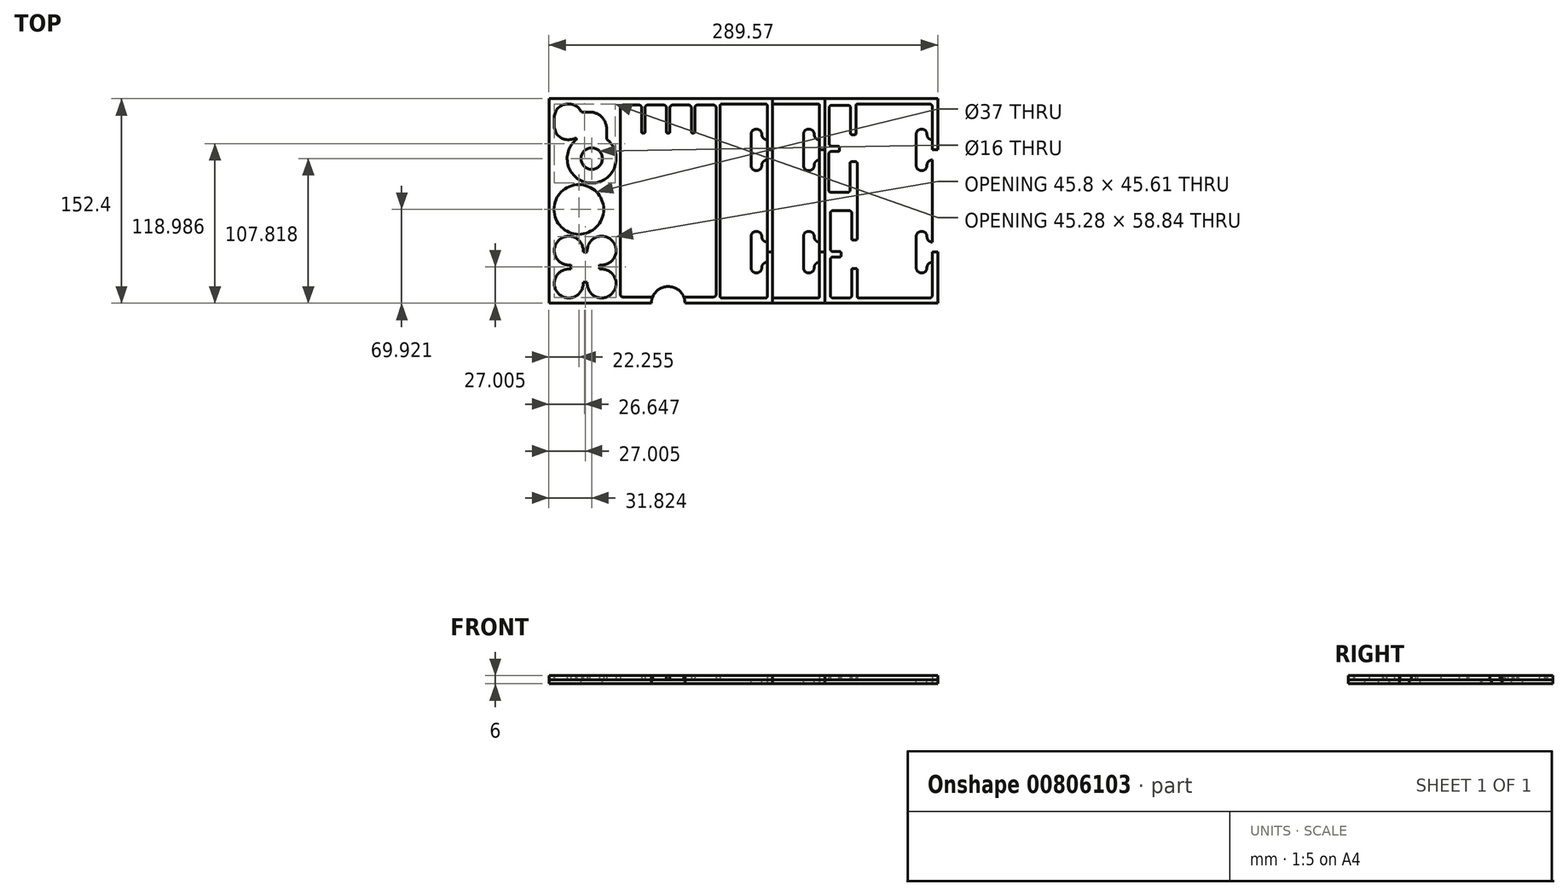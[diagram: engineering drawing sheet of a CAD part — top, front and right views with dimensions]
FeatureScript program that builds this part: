
annotation { "Feature Type Name" : "Feature", "Feature Type Description" : "" }
export const myFeature = defineFeature(function(context is Context, id is Id, definition is map)
    precondition{}
    {
        {
            var Q0;
            Q0=qCreatedBy(makeId("Top.planeOp"),FACE);
            var sketch = newSketch(context, id + "F0", { "sketchPlane" : qUnion([Q0])});
            skLineSegment(sketch, "E0.bottom", {"start": v(-142.07, 76.21) * mm, "end": v(147.5, 76.21) * mm});
            skLineSegment(sketch, "E0.top", {"start": v(-142.07, -76.19) * mm, "end": v(147.5, -76.19) * mm});
            skCircle(sketch, "E1", {"center": v(-127.32, -61.44) * mm, "radius": 10.75 * mm});
            skCircle(sketch, "E2", {"center": v(-102.82, -61.44) * mm, "radius": 10.75 * mm});
            skCircle(sketch, "E3", {"center": v(-127.32, -36.94) * mm, "radius": 10.75 * mm});
            skCircle(sketch, "E4", {"center": v(-102.82, -36.94) * mm, "radius": 10.75 * mm});
            skCircle(sketch, "E5", {"center": v(-119.82, -6.27) * mm, "radius": 18.5 * mm});
            skCircle(sketch, "E6", {"center": v(-115.07, -49.79) * mm, "radius": 10.75 * mm});
            skLineSegment(sketch, "E7", {"start": v(-138.07, 62.21) * mm, "end": v(-138.07, 55.71) * mm});
            skLineSegment(sketch, "E8", {"start": v(-117.07, 62.21) * mm, "end": v(-117.07, 55.71) * mm});
            skLineSegment(sketch, "E9", {"start": v(-128.07, 72.21) * mm, "end": v(-127.07, 72.21) * mm});
            skLineSegment(sketch, "E10", {"start": v(-128.07, 45.71) * mm, "end": v(-127.07, 45.71) * mm});
            skArc(sketch, "E11.filletArc", {"start": v(-128.07, 72.21) * mm, "mid": v(-135.14, 69.28) * mm, "end": v(-138.07, 62.21) * mm});
            skArc(sketch, "E12.filletArc", {"start": v(-117.07, 62.21) * mm, "mid": v(-120, 69.28) * mm, "end": v(-127.07, 72.21) * mm});
            skArc(sketch, "E13.filletArc", {"start": v(-127.07, 45.71) * mm, "mid": v(-120, 48.64) * mm, "end": v(-117.07, 55.71) * mm});
            skArc(sketch, "E14.filletArc", {"start": v(-138.07, 55.71) * mm, "mid": v(-135.14, 48.64) * mm, "end": v(-128.07, 45.71) * mm});
            skCircle(sketch, "E15", {"center": v(-110.25, 31.63) * mm, "radius": 18.25 * mm});
            skCircle(sketch, "E16", {"center": v(-110.25, 31.63) * mm, "radius": 8 * mm});
            skCircle(sketch, "E17", {"center": v(-111.62, 53.78) * mm, "radius": 12.5 * mm});
            skLineSegment(sketch, "E18", {"start": v(-111.83, 66.28) * mm, "end": v(-117.93, 66.28) * mm});
            skLineSegment(sketch, "E19", {"start": v(-99.12, 53.73) * mm, "end": v(-99.12, 46.1) * mm});
            skLineSegment(sketch, "E20", {"start": v(-89, 50.51) * mm, "end": v(-17.5, 50.51) * mm});
            skLineSegment(sketch, "E21", {"start": v(-73, 69.51) * mm, "end": v(-73, 51.51) * mm});
            skLineSegment(sketch, "E22", {"start": v(-70.5, 69.51) * mm, "end": v(-70.5, 51.51) * mm});
            skLineSegment(sketch, "E23", {"start": v(-54.5, 69.51) * mm, "end": v(-54.5, 51.51) * mm});
            skLineSegment(sketch, "E24", {"start": v(-52, 69.51) * mm, "end": v(-52, 51.51) * mm});
            skLineSegment(sketch, "E25", {"start": v(-36, 69.51) * mm, "end": v(-36, 51.51) * mm});
            skLineSegment(sketch, "E26", {"start": v(-33.5, 69.51) * mm, "end": v(-33.5, 51.51) * mm});
            skLineSegment(sketch, "E27", {"start": v(-87, 71.51) * mm, "end": v(-75, 71.51) * mm});
            skLineSegment(sketch, "E28", {"start": v(-68.5, 71.51) * mm, "end": v(-56.5, 71.51) * mm});
            skLineSegment(sketch, "E29", {"start": v(-50, 71.51) * mm, "end": v(-38, 71.51) * mm});
            skLineSegment(sketch, "E30", {"start": v(-19.5, 71.51) * mm, "end": v(-31.5, 71.51) * mm});
            skArc(sketch, "E31.filletArc", {"start": v(-87, 71.51) * mm, "mid": v(-88.41, 70.93) * mm, "end": v(-89, 69.51) * mm});
            skArc(sketch, "E32.filletArc", {"start": v(-73, 69.51) * mm, "mid": v(-73.58, 70.93) * mm, "end": v(-75, 71.51) * mm});
            skArc(sketch, "E33.filletArc", {"start": v(-68.5, 71.51) * mm, "mid": v(-69.91, 70.93) * mm, "end": v(-70.5, 69.51) * mm});
            skArc(sketch, "E34.filletArc", {"start": v(-54.5, 69.51) * mm, "mid": v(-55.08, 70.93) * mm, "end": v(-56.5, 71.51) * mm});
            skArc(sketch, "E35.filletArc", {"start": v(-50, 71.51) * mm, "mid": v(-51.41, 70.93) * mm, "end": v(-52, 69.51) * mm});
            skArc(sketch, "E36.filletArc", {"start": v(-36, 69.51) * mm, "mid": v(-36.58, 70.93) * mm, "end": v(-38, 71.51) * mm});
            skArc(sketch, "E37.filletArc", {"start": v(-31.5, 71.51) * mm, "mid": v(-32.91, 70.93) * mm, "end": v(-33.5, 69.51) * mm});
            skArc(sketch, "E38.filletArc", {"start": v(-17.5, 69.51) * mm, "mid": v(-18.08, 70.93) * mm, "end": v(-19.5, 71.51) * mm});
            skArc(sketch, "E39.filletArc", {"start": v(-89, -69.49) * mm, "mid": v(-88.41, -70.9) * mm, "end": v(-87, -71.49) * mm});
            skArc(sketch, "E40.filletArc", {"start": v(-19.5, -71.49) * mm, "mid": v(-18.08, -70.9) * mm, "end": v(-17.5, -69.49) * mm});
            skArc(sketch, "E41.filletArc", {"start": v(-73, 51.51) * mm, "mid": v(-72.7, 50.8) * mm, "end": v(-72, 50.51) * mm});
            skArc(sketch, "E42.filletArc", {"start": v(-71.5, 50.51) * mm, "mid": v(-70.79, 50.8) * mm, "end": v(-70.5, 51.51) * mm});
            skArc(sketch, "E43.filletArc", {"start": v(-54.5, 51.51) * mm, "mid": v(-54.2, 50.8) * mm, "end": v(-53.5, 50.51) * mm});
            skArc(sketch, "E44.filletArc", {"start": v(-53, 50.51) * mm, "mid": v(-52.29, 50.8) * mm, "end": v(-52, 51.51) * mm});
            skArc(sketch, "E45.filletArc", {"start": v(-36, 51.51) * mm, "mid": v(-35.7, 50.8) * mm, "end": v(-35, 50.51) * mm});
            skArc(sketch, "E46.filletArc", {"start": v(-34.5, 50.51) * mm, "mid": v(-33.79, 50.8) * mm, "end": v(-33.5, 51.51) * mm});
            skLineSegment(sketch, "E47", {"start": v(-89, 69.51) * mm, "end": v(-89, 50.51) * mm});
            skLineSegment(sketch, "E48", {"start": v(-17.5, 69.51) * mm, "end": v(-17.5, 50.51) * mm});
            skLineSegment(sketch, "E49", {"start": v(-89, 50.51) * mm, "end": v(-89, -69.49) * mm});
            skLineSegment(sketch, "E50", {"start": v(-17.5, -69.49) * mm, "end": v(-17.5, 50.51) * mm});
            skArc(sketch, "E51", {"start": v(-40.75, -76.19) * mm, "mid": v(-53.25, -63.69) * mm, "end": v(-65.75, -76.19) * mm});
            skLineSegment(sketch, "E52", {"start": v(-87, -71.49) * mm, "end": v(-64.83, -71.49) * mm});
            skLineSegment(sketch, "E53", {"start": v(-19.5, -71.49) * mm, "end": v(-41.66, -71.49) * mm});
            skLineSegment(sketch, "E54", {"start": v(20.5, 71.21) * mm, "end": v(20.5, -71.19) * mm});
            skLineSegment(sketch, "E55", {"start": v(-14.5, 71.21) * mm, "end": v(-14.5, -71.19) * mm});
            skLineSegment(sketch, "E56", {"start": v(59.5, 71.21) * mm, "end": v(59.5, -71.19) * mm});
            skLineSegment(sketch, "E57", {"start": v(63.5, 72.21) * mm, "end": v(63.5, 76.21) * mm});
            skLineSegment(sketch, "E58", {"start": v(63.5, -72.19) * mm, "end": v(63.5, -76.19) * mm});
            skLineSegment(sketch, "E59", {"start": v(68.6, 71.37) * mm, "end": v(80.66, 71.37) * mm});
            skLineSegment(sketch, "E60", {"start": v(69.5, -72.19) * mm, "end": v(81.5, -72.19) * mm});
            skLineSegment(sketch, "E61", {"start": v(68.26, 6.37) * mm, "end": v(80.26, 6.37) * mm});
            skLineSegment(sketch, "E62", {"start": v(81.5, -7.19) * mm, "end": v(69.5, -7.19) * mm});
            skLineSegment(sketch, "E63", {"start": v(83.5, -28.19) * mm, "end": v(83.5, -9.19) * mm});
            skLineSegment(sketch, "E64", {"start": v(82.66, 69.37) * mm, "end": v(82.66, 50.37) * mm});
            skLineSegment(sketch, "E65", {"start": v(83.66, 49.37) * mm, "end": v(85.66, 49.37) * mm});
            skLineSegment(sketch, "E66", {"start": v(86.66, 50.37) * mm, "end": v(86.66, 71.21) * mm});
            skLineSegment(sketch, "E67", {"start": v(73.26, 36.87) * mm, "end": v(68.26, 36.87) * mm});
            skLineSegment(sketch, "E68", {"start": v(69.5, -37.69) * mm, "end": v(74.5, -37.69) * mm});
            skLineSegment(sketch, "E69", {"start": v(75.5, -38.69) * mm, "end": v(75.5, -40.69) * mm});
            skLineSegment(sketch, "E70", {"start": v(74.5, -41.69) * mm, "end": v(69.5, -41.69) * mm});
            skLineSegment(sketch, "E71", {"start": v(83.5, -70.19) * mm, "end": v(83.5, -51.19) * mm});
            skLineSegment(sketch, "E72", {"start": v(84.5, -50.19) * mm, "end": v(86.5, -50.19) * mm});
            skLineSegment(sketch, "E73", {"start": v(87.5, -51.19) * mm, "end": v(87.5, -71.19) * mm});
            skArc(sketch, "E74.filletArc", {"start": v(68.6, 71.37) * mm, "mid": v(67.38, 70.95) * mm, "end": v(66.66, 69.87) * mm});
            skArc(sketch, "E75.filletArc", {"start": v(82.66, 69.37) * mm, "mid": v(82.08, 70.79) * mm, "end": v(80.66, 71.37) * mm});
            skArc(sketch, "E76.filletArc", {"start": v(66.66, 42.72) * mm, "mid": v(67.3, 41.4) * mm, "end": v(68.66, 40.87) * mm});
            skLineSegment(sketch, "E77", {"start": v(66.26, 34.87) * mm, "end": v(66.26, 8.37) * mm});
            skArc(sketch, "E78.filletArc", {"start": v(68.26, 36.87) * mm, "mid": v(66.85, 36.29) * mm, "end": v(66.26, 34.87) * mm});
            skArc(sketch, "E79.filletArc", {"start": v(66.26, 8.37) * mm, "mid": v(66.85, 6.96) * mm, "end": v(68.26, 6.37) * mm});
            skArc(sketch, "E80.filletArc", {"start": v(80.26, 6.37) * mm, "mid": v(81.68, 6.96) * mm, "end": v(82.26, 8.37) * mm});
            skLineSegment(sketch, "E81", {"start": v(67.5, -9.19) * mm, "end": v(67.5, -35.69) * mm});
            skLineSegment(sketch, "E82", {"start": v(67.5, -43.69) * mm, "end": v(67.5, -70.19) * mm});
            skArc(sketch, "E83.filletArc", {"start": v(83.5, -9.19) * mm, "mid": v(82.92, -7.77) * mm, "end": v(81.5, -7.19) * mm});
            skArc(sketch, "E84.filletArc", {"start": v(69.5, -7.19) * mm, "mid": v(68.09, -7.77) * mm, "end": v(67.5, -9.19) * mm});
            skArc(sketch, "E85.filletArc", {"start": v(67.5, -35.69) * mm, "mid": v(68.09, -37.1) * mm, "end": v(69.5, -37.69) * mm});
            skArc(sketch, "E86.filletArc", {"start": v(69.5, -41.69) * mm, "mid": v(68.09, -42.27) * mm, "end": v(67.5, -43.69) * mm});
            skArc(sketch, "E87.filletArc", {"start": v(67.5, -70.19) * mm, "mid": v(68.09, -71.6) * mm, "end": v(69.5, -72.19) * mm});
            skArc(sketch, "E88.filletArc", {"start": v(81.5, -72.19) * mm, "mid": v(82.92, -71.6) * mm, "end": v(83.5, -70.19) * mm});
            skLineSegment(sketch, "E89", {"start": v(88.5, -72.19) * mm, "end": v(141.5, -72.19) * mm});
            skLineSegment(sketch, "E90", {"start": v(87.66, 72.21) * mm, "end": v(141.5, 72.21) * mm});
            skArc(sketch, "E91.filletArc", {"start": v(143.5, 70.21) * mm, "mid": v(142.92, 71.63) * mm, "end": v(141.5, 72.21) * mm});
            skArc(sketch, "E92.filletArc", {"start": v(141.5, -72.19) * mm, "mid": v(142.92, -71.6) * mm, "end": v(143.5, -70.19) * mm});
            skArc(sketch, "E93.filletArc", {"start": v(87.5, -71.19) * mm, "mid": v(87.8, -71.9) * mm, "end": v(88.5, -72.19) * mm});
            skArc(sketch, "E94.filletArc", {"start": v(87.66, 72.21) * mm, "mid": v(86.96, 71.92) * mm, "end": v(86.66, 71.21) * mm});
            skArc(sketch, "E95.filletArc", {"start": v(85.66, 49.37) * mm, "mid": v(86.37, 49.67) * mm, "end": v(86.66, 50.37) * mm});
            skArc(sketch, "E96.filletArc", {"start": v(82.66, 50.37) * mm, "mid": v(82.96, 49.67) * mm, "end": v(83.66, 49.37) * mm});
            skArc(sketch, "E97.filletArc", {"start": v(74.26, 39.87) * mm, "mid": v(74.12, 40.47) * mm, "end": v(73.66, 40.87) * mm});
            skArc(sketch, "E98.filletArc", {"start": v(73.26, 36.87) * mm, "mid": v(73.97, 37.17) * mm, "end": v(74.26, 37.87) * mm});
            skArc(sketch, "E99.filletArc", {"start": v(83.5, -28.19) * mm, "mid": v(83.8, -28.9) * mm, "end": v(84.5, -29.19) * mm});
            skArc(sketch, "E100.filletArc", {"start": v(75.5, -38.69) * mm, "mid": v(75.21, -37.98) * mm, "end": v(74.5, -37.69) * mm});
            skArc(sketch, "E101.filletArc", {"start": v(74.5, -41.69) * mm, "mid": v(75.21, -41.4) * mm, "end": v(75.5, -40.69) * mm});
            skArc(sketch, "E102.filletArc", {"start": v(84.5, -50.19) * mm, "mid": v(83.8, -50.48) * mm, "end": v(83.5, -51.19) * mm});
            skArc(sketch, "E103.filletArc", {"start": v(87.5, -51.19) * mm, "mid": v(87.21, -50.48) * mm, "end": v(86.5, -50.19) * mm});
            skLineSegment(sketch, "E104", {"start": v(66.66, 69.87) * mm, "end": v(66.66, 42.72) * mm});
            skLineSegment(sketch, "E105", {"start": v(68.66, 40.87) * mm, "end": v(73.66, 40.87) * mm});
            skLineSegment(sketch, "E106", {"start": v(74.26, 39.87) * mm, "end": v(74.26, 37.87) * mm});
            skLineSegment(sketch, "E107", {"start": v(-13.5, 72.21) * mm, "end": v(19.5, 72.21) * mm});
            skLineSegment(sketch, "E108", {"start": v(-13.5, -72.19) * mm, "end": v(19.5, -72.19) * mm});
            skLineSegment(sketch, "E109", {"start": v(58.5, 72.21) * mm, "end": v(25.5, 72.21) * mm});
            skLineSegment(sketch, "E110", {"start": v(58.5, -72.19) * mm, "end": v(25.5, -72.19) * mm});
            skLineSegment(sketch, "E111", {"start": v(143.5, 70.21) * mm, "end": v(143.5, -70.19) * mm});
            skPoint(sketch, "E112.visualSharp", {"position": v(-14.5, 72.21) * mm});
            skArc(sketch, "E112.filletArc", {"start": v(-13.5, 72.21) * mm, "mid": v(-14.2, 71.92) * mm, "end": v(-14.5, 71.21) * mm});
            skPoint(sketch, "E113.visualSharp", {"position": v(20.5, 72.21) * mm});
            skArc(sketch, "E113.filletArc", {"start": v(20.5, 71.21) * mm, "mid": v(20.21, 71.92) * mm, "end": v(19.5, 72.21) * mm});
            skPoint(sketch, "E114.visualSharp", {"position": v(-14.5, -72.19) * mm});
            skArc(sketch, "E114.filletArc", {"start": v(-14.5, -71.19) * mm, "mid": v(-14.2, -71.9) * mm, "end": v(-13.5, -72.19) * mm});
            skPoint(sketch, "E115.visualSharp", {"position": v(20.5, -72.19) * mm});
            skArc(sketch, "E115.filletArc", {"start": v(19.5, -72.19) * mm, "mid": v(20.21, -71.9) * mm, "end": v(20.5, -71.19) * mm});
            skPoint(sketch, "E116.visualSharp", {"position": v(24.5, -72.19) * mm});
            skPoint(sketch, "E117.visualSharp", {"position": v(59.5, -72.19) * mm});
            skArc(sketch, "E117.filletArc", {"start": v(58.5, -72.19) * mm, "mid": v(59.21, -71.9) * mm, "end": v(59.5, -71.19) * mm});
            skPoint(sketch, "E118.visualSharp", {"position": v(24.5, 72.21) * mm});
            skPoint(sketch, "E119.visualSharp", {"position": v(59.5, 72.21) * mm});
            skArc(sketch, "E119.filletArc", {"start": v(59.5, 71.21) * mm, "mid": v(59.21, 71.92) * mm, "end": v(58.5, 72.21) * mm});
            skLineSegment(sketch, "E120", {"start": v(-142.07, 38.11) * mm, "end": v(147.5, 38.11) * mm});
            skLineSegment(sketch, "E121", {"start": v(147.5, -38.09) * mm, "end": v(-142.07, -38.09) * mm});
            skArc(sketch, "E122.filletArc", {"start": v(87.5, 28.21) * mm, "mid": v(87.22, 28.92) * mm, "end": v(86.51, 29.21) * mm});
            skLineSegment(sketch, "E123", {"start": v(87.5, 28.21) * mm, "end": v(87.5, -28.19) * mm});
            skLineSegment(sketch, "E124", {"start": v(86.5, -29.19) * mm, "end": v(84.5, -29.19) * mm});
            skPoint(sketch, "E125.visualSharp", {"position": v(87.5, -29.19) * mm});
            skArc(sketch, "E125.filletArc", {"start": v(86.5, -29.19) * mm, "mid": v(87.22, -28.9) * mm, "end": v(87.5, -28.19) * mm});
            skPoint(sketch, "E126", {"position": v(-158.07, 38.11) * mm});
            skLineSegment(sketch, "E127", {"start": v(-158.07, 38.11) * mm, "end": v(-158.07, 49.61) * mm});
            skLineSegment(sketch, "E128", {"start": v(-158.07, 38.11) * mm, "end": v(-158.07, 26.61) * mm});
            skArc(sketch, "E129.filletArc", {"start": v(-154.07, 53.61) * mm, "mid": v(-156.9, 52.44) * mm, "end": v(-158.07, 49.61) * mm});
            skArc(sketch, "E130.filletArc", {"start": v(-150.07, 49.61) * mm, "mid": v(-151.24, 52.44) * mm, "end": v(-154.07, 53.61) * mm});
            skArc(sketch, "E131.filletArc", {"start": v(-150.07, 49.61) * mm, "mid": v(-148.9, 46.79) * mm, "end": v(-146.07, 45.61) * mm});
            skArc(sketch, "E132.filletArc", {"start": v(-146.07, 30.61) * mm, "mid": v(-148.9, 29.44) * mm, "end": v(-150.07, 26.61) * mm});
            skArc(sketch, "E133.filletArc", {"start": v(-154.07, 22.61) * mm, "mid": v(-151.24, 23.79) * mm, "end": v(-150.07, 26.61) * mm});
            skArc(sketch, "E134.filletArc", {"start": v(-158.07, 26.61) * mm, "mid": v(-156.9, 23.79) * mm, "end": v(-154.07, 22.61) * mm});
            skArc(sketch, "E135.filletArc", {"start": v(-146.07, 45.61) * mm, "mid": v(-143.24, 46.79) * mm, "end": v(-142.07, 49.61) * mm});
            skArc(sketch, "E136.filletArc", {"start": v(-142.07, 26.61) * mm, "mid": v(-143.24, 29.44) * mm, "end": v(-146.07, 30.61) * mm});
            skPoint(sketch, "E137", {"position": v(-142.07, 38.11) * mm});
            skPoint(sketch, "E138", {"position": v(-158.07, -38.09) * mm});
            skLineSegment(sketch, "E139", {"start": v(-158.07, -38.09) * mm, "end": v(-158.07, -26.59) * mm});
            skLineSegment(sketch, "E140", {"start": v(-158.07, -38.09) * mm, "end": v(-158.07, -49.59) * mm});
            skArc(sketch, "E141.filletArc", {"start": v(-154.07, -22.59) * mm, "mid": v(-156.9, -23.76) * mm, "end": v(-158.07, -26.59) * mm});
            skArc(sketch, "E142.filletArc", {"start": v(-150.07, -26.59) * mm, "mid": v(-151.24, -23.76) * mm, "end": v(-154.07, -22.59) * mm});
            skArc(sketch, "E143.filletArc", {"start": v(-150.07, -26.59) * mm, "mid": v(-148.9, -29.41) * mm, "end": v(-146.07, -30.59) * mm});
            skArc(sketch, "E144.filletArc", {"start": v(-146.07, -45.59) * mm, "mid": v(-148.9, -46.76) * mm, "end": v(-150.07, -49.59) * mm});
            skArc(sketch, "E145.filletArc", {"start": v(-154.07, -53.59) * mm, "mid": v(-151.24, -52.41) * mm, "end": v(-150.07, -49.59) * mm});
            skArc(sketch, "E146.filletArc", {"start": v(-158.07, -49.59) * mm, "mid": v(-156.9, -52.41) * mm, "end": v(-154.07, -53.59) * mm});
            skArc(sketch, "E147.filletArc", {"start": v(-146.07, -30.59) * mm, "mid": v(-143.24, -29.41) * mm, "end": v(-142.07, -26.59) * mm});
            skArc(sketch, "E148.filletArc", {"start": v(-142.07, -49.59) * mm, "mid": v(-143.24, -46.76) * mm, "end": v(-146.07, -45.59) * mm});
            skPoint(sketch, "E149", {"position": v(-142.07, -38.09) * mm});
            skPoint(sketch, "E150", {"position": v(8.5, 38.11) * mm});
            skLineSegment(sketch, "E151", {"start": v(8.5, 38.11) * mm, "end": v(8.5, 49.61) * mm});
            skLineSegment(sketch, "E152", {"start": v(8.5, 38.11) * mm, "end": v(8.5, 26.61) * mm});
            skArc(sketch, "E153.filletArc", {"start": v(12.5, 53.61) * mm, "mid": v(9.68, 52.44) * mm, "end": v(8.5, 49.61) * mm});
            skArc(sketch, "E154.filletArc", {"start": v(16.5, 49.61) * mm, "mid": v(15.33, 52.44) * mm, "end": v(12.5, 53.61) * mm});
            skArc(sketch, "E155.filletArc", {"start": v(16.5, 49.61) * mm, "mid": v(17.68, 46.79) * mm, "end": v(20.5, 45.61) * mm});
            skArc(sketch, "E156.filletArc", {"start": v(20.5, 30.61) * mm, "mid": v(17.68, 29.44) * mm, "end": v(16.5, 26.61) * mm});
            skArc(sketch, "E157.filletArc", {"start": v(12.5, 22.61) * mm, "mid": v(15.33, 23.79) * mm, "end": v(16.5, 26.61) * mm});
            skArc(sketch, "E158.filletArc", {"start": v(8.5, 26.61) * mm, "mid": v(9.68, 23.79) * mm, "end": v(12.5, 22.61) * mm});
            skArc(sketch, "E159.filletArc", {"start": v(20.5, 45.61) * mm, "mid": v(23.33, 46.79) * mm, "end": v(24.5, 49.61) * mm});
            skArc(sketch, "E160.filletArc", {"start": v(24.5, 26.61) * mm, "mid": v(23.33, 29.44) * mm, "end": v(20.5, 30.61) * mm});
            skPoint(sketch, "E161", {"position": v(24.5, 38.11) * mm});
            skPoint(sketch, "E162", {"position": v(8.5, -38.09) * mm});
            skLineSegment(sketch, "E163", {"start": v(8.5, -38.09) * mm, "end": v(8.5, -26.59) * mm});
            skLineSegment(sketch, "E164", {"start": v(8.5, -38.09) * mm, "end": v(8.5, -49.59) * mm});
            skArc(sketch, "E165.filletArc", {"start": v(12.5, -22.59) * mm, "mid": v(9.68, -23.76) * mm, "end": v(8.5, -26.59) * mm});
            skArc(sketch, "E166.filletArc", {"start": v(16.5, -26.59) * mm, "mid": v(15.33, -23.76) * mm, "end": v(12.5, -22.59) * mm});
            skArc(sketch, "E167.filletArc", {"start": v(16.5, -26.59) * mm, "mid": v(17.68, -29.41) * mm, "end": v(20.5, -30.59) * mm});
            skArc(sketch, "E168.filletArc", {"start": v(20.5, -45.59) * mm, "mid": v(17.68, -46.76) * mm, "end": v(16.5, -49.59) * mm});
            skArc(sketch, "E169.filletArc", {"start": v(12.5, -53.59) * mm, "mid": v(15.33, -52.41) * mm, "end": v(16.5, -49.59) * mm});
            skArc(sketch, "E170.filletArc", {"start": v(8.5, -49.59) * mm, "mid": v(9.68, -52.41) * mm, "end": v(12.5, -53.59) * mm});
            skArc(sketch, "E171.filletArc", {"start": v(20.5, -30.59) * mm, "mid": v(23.33, -29.41) * mm, "end": v(24.5, -26.59) * mm});
            skArc(sketch, "E172.filletArc", {"start": v(24.5, -49.59) * mm, "mid": v(23.33, -46.76) * mm, "end": v(20.5, -45.59) * mm});
            skPoint(sketch, "E173", {"position": v(24.5, -38.09) * mm});
            skPoint(sketch, "E174", {"position": v(47.5, 38.11) * mm});
            skLineSegment(sketch, "E175", {"start": v(47.5, 38.11) * mm, "end": v(47.5, 49.61) * mm});
            skLineSegment(sketch, "E176", {"start": v(47.5, 38.11) * mm, "end": v(47.5, 26.61) * mm});
            skArc(sketch, "E177.filletArc", {"start": v(51.5, 53.61) * mm, "mid": v(48.68, 52.44) * mm, "end": v(47.5, 49.61) * mm});
            skArc(sketch, "E178.filletArc", {"start": v(55.5, 49.61) * mm, "mid": v(54.33, 52.44) * mm, "end": v(51.5, 53.61) * mm});
            skArc(sketch, "E179.filletArc", {"start": v(55.5, 49.61) * mm, "mid": v(56.68, 46.79) * mm, "end": v(59.5, 45.61) * mm});
            skArc(sketch, "E180.filletArc", {"start": v(59.5, 30.61) * mm, "mid": v(56.68, 29.44) * mm, "end": v(55.5, 26.61) * mm});
            skArc(sketch, "E181.filletArc", {"start": v(51.5, 22.61) * mm, "mid": v(54.33, 23.79) * mm, "end": v(55.5, 26.61) * mm});
            skArc(sketch, "E182.filletArc", {"start": v(47.5, 26.61) * mm, "mid": v(48.68, 23.79) * mm, "end": v(51.5, 22.61) * mm});
            skArc(sketch, "E183.filletArc", {"start": v(59.5, 45.61) * mm, "mid": v(62.33, 46.79) * mm, "end": v(63.5, 49.61) * mm});
            skArc(sketch, "E184.filletArc", {"start": v(63.5, 26.61) * mm, "mid": v(62.33, 29.44) * mm, "end": v(59.5, 30.61) * mm});
            skPoint(sketch, "E185", {"position": v(63.5, 38.11) * mm});
            skPoint(sketch, "E186", {"position": v(47.5, -38.09) * mm});
            skLineSegment(sketch, "E187", {"start": v(47.5, -38.09) * mm, "end": v(47.5, -26.59) * mm});
            skLineSegment(sketch, "E188", {"start": v(47.5, -38.09) * mm, "end": v(47.5, -49.59) * mm});
            skArc(sketch, "E189.filletArc", {"start": v(51.5, -22.59) * mm, "mid": v(48.68, -23.76) * mm, "end": v(47.5, -26.59) * mm});
            skArc(sketch, "E190.filletArc", {"start": v(55.5, -26.59) * mm, "mid": v(54.33, -23.76) * mm, "end": v(51.5, -22.59) * mm});
            skArc(sketch, "E191.filletArc", {"start": v(55.5, -26.59) * mm, "mid": v(56.68, -29.41) * mm, "end": v(59.5, -30.59) * mm});
            skArc(sketch, "E192.filletArc", {"start": v(59.5, -45.59) * mm, "mid": v(56.68, -46.76) * mm, "end": v(55.5, -49.59) * mm});
            skArc(sketch, "E193.filletArc", {"start": v(51.5, -53.59) * mm, "mid": v(54.33, -52.41) * mm, "end": v(55.5, -49.59) * mm});
            skArc(sketch, "E194.filletArc", {"start": v(47.5, -49.59) * mm, "mid": v(48.68, -52.41) * mm, "end": v(51.5, -53.59) * mm});
            skArc(sketch, "E195.filletArc", {"start": v(59.5, -30.59) * mm, "mid": v(62.33, -29.41) * mm, "end": v(63.5, -26.59) * mm});
            skArc(sketch, "E196.filletArc", {"start": v(63.5, -49.59) * mm, "mid": v(62.33, -46.76) * mm, "end": v(59.5, -45.59) * mm});
            skPoint(sketch, "E197", {"position": v(63.5, -38.09) * mm});
            skPoint(sketch, "E198", {"position": v(131.5, 38.11) * mm});
            skLineSegment(sketch, "E199", {"start": v(131.5, 38.11) * mm, "end": v(131.5, 49.61) * mm});
            skLineSegment(sketch, "E200", {"start": v(131.5, 38.11) * mm, "end": v(131.5, 26.61) * mm});
            skArc(sketch, "E201.filletArc", {"start": v(135.5, 53.61) * mm, "mid": v(132.68, 52.44) * mm, "end": v(131.5, 49.61) * mm});
            skArc(sketch, "E202.filletArc", {"start": v(139.5, 49.61) * mm, "mid": v(138.33, 52.44) * mm, "end": v(135.5, 53.61) * mm});
            skArc(sketch, "E203.filletArc", {"start": v(139.5, 49.61) * mm, "mid": v(140.68, 46.79) * mm, "end": v(143.5, 45.61) * mm});
            skArc(sketch, "E204.filletArc", {"start": v(143.5, 30.61) * mm, "mid": v(140.68, 29.44) * mm, "end": v(139.5, 26.61) * mm});
            skArc(sketch, "E205.filletArc", {"start": v(135.5, 22.61) * mm, "mid": v(138.33, 23.79) * mm, "end": v(139.5, 26.61) * mm});
            skArc(sketch, "E206.filletArc", {"start": v(131.5, 26.61) * mm, "mid": v(132.68, 23.79) * mm, "end": v(135.5, 22.61) * mm});
            skArc(sketch, "E207.filletArc", {"start": v(143.5, 45.61) * mm, "mid": v(146.33, 46.79) * mm, "end": v(147.5, 49.61) * mm});
            skArc(sketch, "E208.filletArc", {"start": v(147.5, 26.61) * mm, "mid": v(146.33, 29.44) * mm, "end": v(143.5, 30.61) * mm});
            skPoint(sketch, "E209", {"position": v(147.5, 38.11) * mm});
            skPoint(sketch, "E210", {"position": v(131.5, -38.09) * mm});
            skLineSegment(sketch, "E211", {"start": v(131.5, -38.09) * mm, "end": v(131.5, -26.59) * mm});
            skLineSegment(sketch, "E212", {"start": v(131.5, -38.09) * mm, "end": v(131.5, -49.59) * mm});
            skArc(sketch, "E213.filletArc", {"start": v(135.5, -22.59) * mm, "mid": v(132.68, -23.76) * mm, "end": v(131.5, -26.59) * mm});
            skArc(sketch, "E214.filletArc", {"start": v(139.5, -26.59) * mm, "mid": v(138.33, -23.76) * mm, "end": v(135.5, -22.59) * mm});
            skArc(sketch, "E215.filletArc", {"start": v(139.5, -26.59) * mm, "mid": v(140.68, -29.41) * mm, "end": v(143.5, -30.59) * mm});
            skArc(sketch, "E216.filletArc", {"start": v(143.5, -45.59) * mm, "mid": v(140.68, -46.76) * mm, "end": v(139.5, -49.59) * mm});
            skArc(sketch, "E217.filletArc", {"start": v(135.5, -53.59) * mm, "mid": v(138.33, -52.41) * mm, "end": v(139.5, -49.59) * mm});
            skArc(sketch, "E218.filletArc", {"start": v(131.5, -49.59) * mm, "mid": v(132.68, -52.41) * mm, "end": v(135.5, -53.59) * mm});
            skArc(sketch, "E219.filletArc", {"start": v(143.5, -30.59) * mm, "mid": v(146.33, -29.41) * mm, "end": v(147.5, -26.59) * mm});
            skArc(sketch, "E220.filletArc", {"start": v(147.5, -49.59) * mm, "mid": v(146.33, -46.76) * mm, "end": v(143.5, -45.59) * mm});
            skPoint(sketch, "E221", {"position": v(147.5, -38.09) * mm});
            skLineSegment(sketch, "E222", {"start": v(24.5, 71.21) * mm, "end": v(24.5, 76.21) * mm});
            skLineSegment(sketch, "E223", {"start": v(24.5, -71.19) * mm, "end": v(24.5, -76.19) * mm});
            skLineSegment(sketch, "E224", {"start": v(24.5, 71.21) * mm, "end": v(24.5, -71.19) * mm});
            skLineSegment(sketch, "E225", {"start": v(-142.07, 76.21) * mm, "end": v(-142.07, -76.19) * mm});
            skLineSegment(sketch, "E226", {"start": v(63.5, 72.21) * mm, "end": v(63.5, -72.19) * mm});
            skLineSegment(sketch, "E227", {"start": v(147.5, 76.21) * mm, "end": v(147.5, -76.19) * mm});
            skLineSegment(sketch, "E228", {"start": v(25.5, 72.21) * mm, "end": v(24.5, 72.21) * mm});
            skLineSegment(sketch, "E229", {"start": v(25.5, -72.19) * mm, "end": v(24.5, -72.19) * mm});
            skLineSegment(sketch, "E230", {"start": v(82.26, 8.37) * mm, "end": v(82.26, 28.21) * mm});
            skLineSegment(sketch, "E231", {"start": v(83.26, 29.21) * mm, "end": v(86.51, 29.21) * mm});
            skPoint(sketch, "E232.visualSharp", {"position": v(82.26, 29.21) * mm});
            skArc(sketch, "E232.filletArc", {"start": v(83.26, 29.21) * mm, "mid": v(82.56, 28.92) * mm, "end": v(82.26, 28.21) * mm});
            skSolve(sketch);
        }
        {
            var Q0;
            {var subQ0=sQuery(id+"F0.wireOp",EDGE,"E6");var subQ1=sQuery(id+"F0.wireOp",EDGE,"E1");var subQ2=makeQuery(id+"F0.imprint","INTERSECT",VERTEX,{"disambiguationData":[OD(0.0)],"derivedFrom":[subQ1,subQ0]});Q0=makeQuery(id+"F0.imprint","IMPRINT",FACE,{"disambiguationData":[TD([[makeQuery(id+"F0.imprint","IMPRINT",EDGE,{"disambiguationData":[TD([[subQ2,1.0]])],"derivedFrom":subQ1}),1.0]])]});}
            var Q1;
            {var subQ0=sQuery(id+"F0.wireOp",EDGE,"E39.filletArc");Q1=makeQuery(id+"F0.imprint","IMPRINT",FACE,{"disambiguationData":[TD([[makeQuery(id+"F0.imprint","IMPRINT",EDGE,{"derivedFrom":subQ0}),-1.0]])]});}
            var Q2;
            Q2=makeQuery(id+"F0.imprint","IMPRINT",FACE,{"disambiguationData":[TD([[makeQuery(id+"F0.imprint","IMPRINT",EDGE,{"derivedFrom":sQuery(id+"F0.wireOp",EDGE,"E5")}),-1.0]])]});
            var Q3;
            Q3=makeQuery(id+"F0.imprint","IMPRINT",FACE,{"disambiguationData":[TD([[makeQuery(id+"F0.imprint","IMPRINT",EDGE,{"derivedFrom":sQuery(id+"F0.wireOp",EDGE,"E7")}),1.0]])]});
            var Q4;
            {var subQ7=sQuery(id+"F0.wireOp",EDGE,"E152");Q4=makeQuery(id+"F0.imprint","IMPRINT",FACE,{"disambiguationData":[TD([[makeQuery(id+"F0.imprint","IMPRINT",EDGE,{"derivedFrom":subQ7}),-1.0]])]});}
            var Q5;
            Q5=makeQuery(id+"F0.imprint","IMPRINT",FACE,{"disambiguationData":[TD([[makeQuery(id+"F0.imprint","IMPRINT",EDGE,{"derivedFrom":sQuery(id+"F0.wireOp",EDGE,"E24")}),1.0]])]});
            var Q6;
            Q6=makeQuery(id+"F0.imprint","IMPRINT",FACE,{"disambiguationData":[TD([[makeQuery(id+"F0.imprint","IMPRINT",EDGE,{"derivedFrom":sQuery(id+"F0.wireOp",EDGE,"E21")}),-1.0]])]});
            var Q7;
            Q7=makeQuery(id+"F0.imprint","IMPRINT",FACE,{"disambiguationData":[TD([[makeQuery(id+"F0.imprint","IMPRINT",EDGE,{"derivedFrom":sQuery(id+"F0.wireOp",EDGE,"E22")}),1.0]])]});
            var Q8;
            Q8=makeQuery(id+"F0.imprint","IMPRINT",FACE,{"disambiguationData":[TD([[makeQuery(id+"F0.imprint","IMPRINT",EDGE,{"derivedFrom":sQuery(id+"F0.wireOp",EDGE,"E139")}),-1.0]])]});
            var Q9;
            Q9=makeQuery(id+"F0.imprint","IMPRINT",FACE,{"disambiguationData":[TD([[makeQuery(id+"F0.imprint","IMPRINT",EDGE,{"derivedFrom":sQuery(id+"F0.wireOp",EDGE,"E5")}),1.0]])]});
            var Q10;
            {var subQ0=sQuery(id+"F0.wireOp",EDGE,"E6");var subQ10=sQuery(id+"F0.wireOp",EDGE,"E1");var subQ11=makeQuery(id+"F0.imprint","INTERSECT",VERTEX,{"disambiguationData":[OD(0.0)],"derivedFrom":[subQ10,subQ0]});Q10=makeQuery(id+"F0.imprint","IMPRINT",FACE,{"disambiguationData":[TD([[makeQuery(id+"F0.imprint","IMPRINT",EDGE,{"disambiguationData":[TD([[subQ11,1.0]])],"derivedFrom":subQ10}),-1.0]])]});}
            var Q11;
            {var subQ0=sQuery(id+"F0.wireOp",EDGE,"E6");var subQ1=sQuery(id+"F0.wireOp",EDGE,"E3");var subQ2=makeQuery(id+"F0.imprint","INTERSECT",VERTEX,{"disambiguationData":[OD(0.0)],"derivedFrom":[subQ1,subQ0]});Q11=makeQuery(id+"F0.imprint","IMPRINT",FACE,{"disambiguationData":[TD([[makeQuery(id+"F0.imprint","IMPRINT",EDGE,{"disambiguationData":[TD([[subQ2,1.0]])],"derivedFrom":subQ1}),1.0]])]});}
            var Q12;
            {var subQ0=sQuery(id+"F0.wireOp",EDGE,"E120");var subQ1=sQuery(id+"F0.wireOp",EDGE,"E15");var subQ2=makeQuery(id+"F0.imprint","INTERSECT",VERTEX,{"disambiguationData":[OD(0.0)],"derivedFrom":[subQ1,subQ0]});Q12=makeQuery(id+"F0.imprint","IMPRINT",FACE,{"disambiguationData":[TD([[makeQuery(id+"F0.imprint","IMPRINT",EDGE,{"disambiguationData":[TD([[subQ2,1.0]])],"derivedFrom":subQ1}),1.0]])]});}
            var Q13;
            Q13=makeQuery(id+"F0.imprint","IMPRINT",FACE,{"disambiguationData":[TD([[makeQuery(id+"F0.imprint","IMPRINT",EDGE,{"derivedFrom":sQuery(id+"F0.wireOp",EDGE,"E127")}),-1.0]])]});
            var Q14;
            Q14=makeQuery(id+"F0.imprint","IMPRINT",FACE,{"disambiguationData":[TD([[makeQuery(id+"F0.imprint","IMPRINT",EDGE,{"derivedFrom":sQuery(id+"F0.wireOp",EDGE,"E26")}),1.0]])]});
            var Q15;
            Q15=makeQuery(id+"F0.imprint","IMPRINT",FACE,{"disambiguationData":[TD([[makeQuery(id+"F0.imprint","IMPRINT",EDGE,{"derivedFrom":sQuery(id+"F0.wireOp",EDGE,"E108")}),1.0]])]});
            var Q16;
            {var subQ0=sQuery(id+"F0.wireOp",EDGE,"E20");var subQ8=makeQuery(id+"F0.imprint","INTERSECT",VERTEX,{"derivedFrom":[subQ0,sQuery(id+"F0.wireOp",EDGE,"E41.filletArc")]});Q16=makeQuery(id+"F0.imprint","IMPRINT",FACE,{"disambiguationData":[TD([[makeQuery(id+"F0.imprint","IMPRINT",EDGE,{"disambiguationData":[TD([[subQ8,-1.0]])],"derivedFrom":subQ0}),-1.0]])]});}
            var Q17;
            {var subQ0=sQuery(id+"F0.wireOp",EDGE,"E6");var subQ1=sQuery(id+"F0.wireOp",EDGE,"E1");var subQ2=makeQuery(id+"F0.imprint","INTERSECT",VERTEX,{"disambiguationData":[OD(0.0)],"derivedFrom":[subQ1,subQ0]});Q17=makeQuery(id+"F0.imprint","IMPRINT",FACE,{"disambiguationData":[TD([[makeQuery(id+"F0.imprint","IMPRINT",EDGE,{"disambiguationData":[TD([[subQ2,-1.0]])],"derivedFrom":subQ1}),1.0]])]});}
            var Q18;
            {var subQ0=sQuery(id+"F0.wireOp",EDGE,"E6");var subQ1=sQuery(id+"F0.wireOp",EDGE,"E2");var subQ2=makeQuery(id+"F0.imprint","INTERSECT",VERTEX,{"disambiguationData":[OD(0.0)],"derivedFrom":[subQ1,subQ0]});Q18=makeQuery(id+"F0.imprint","IMPRINT",FACE,{"disambiguationData":[TD([[makeQuery(id+"F0.imprint","IMPRINT",EDGE,{"disambiguationData":[TD([[subQ2,1.0]])],"derivedFrom":subQ1}),1.0]])]});}
            var Q19;
            {var subQ0=sQuery(id+"F0.wireOp",EDGE,"E6");var subQ1=sQuery(id+"F0.wireOp",EDGE,"E2");var subQ2=makeQuery(id+"F0.imprint","INTERSECT",VERTEX,{"disambiguationData":[OD(0.0)],"derivedFrom":[subQ1,subQ0]});Q19=makeQuery(id+"F0.imprint","IMPRINT",FACE,{"disambiguationData":[TD([[makeQuery(id+"F0.imprint","IMPRINT",EDGE,{"disambiguationData":[TD([[subQ2,-1.0]])],"derivedFrom":subQ1}),1.0]])]});}
            var Q20;
            {var subQ0=sQuery(id+"F0.wireOp",EDGE,"E6");var subQ1=sQuery(id+"F0.wireOp",EDGE,"E3");var subQ2=makeQuery(id+"F0.imprint","INTERSECT",VERTEX,{"disambiguationData":[OD(0.0)],"derivedFrom":[subQ1,subQ0]});Q20=makeQuery(id+"F0.imprint","IMPRINT",FACE,{"disambiguationData":[TD([[makeQuery(id+"F0.imprint","IMPRINT",EDGE,{"disambiguationData":[TD([[subQ2,-1.0]])],"derivedFrom":subQ1}),1.0]])]});}
            var Q21;
            {var subQ0=sQuery(id+"F0.wireOp",EDGE,"E121");var subQ1=sQuery(id+"F0.wireOp",EDGE,"E3");var subQ2=makeQuery(id+"F0.imprint","INTERSECT",VERTEX,{"disambiguationData":[OD(0.0)],"derivedFrom":[subQ1,subQ0]});Q21=makeQuery(id+"F0.imprint","IMPRINT",FACE,{"disambiguationData":[TD([[makeQuery(id+"F0.imprint","IMPRINT",EDGE,{"disambiguationData":[TD([[subQ2,1.0]])],"derivedFrom":subQ1}),1.0]])]});}
            var Q22;
            {var subQ0=sQuery(id+"F0.wireOp",EDGE,"E6");var subQ1=sQuery(id+"F0.wireOp",EDGE,"E4");var subQ2=makeQuery(id+"F0.imprint","INTERSECT",VERTEX,{"disambiguationData":[OD(0.0)],"derivedFrom":[subQ1,subQ0]});Q22=makeQuery(id+"F0.imprint","IMPRINT",FACE,{"disambiguationData":[TD([[makeQuery(id+"F0.imprint","IMPRINT",EDGE,{"disambiguationData":[TD([[subQ2,-1.0]])],"derivedFrom":subQ1}),1.0]])]});}
            var Q23;
            {var subQ0=sQuery(id+"F0.wireOp",EDGE,"E121");var subQ1=sQuery(id+"F0.wireOp",EDGE,"E50");var subQ2=makeQuery(id+"F0.imprint","INTERSECT",VERTEX,{"derivedFrom":[subQ1,subQ0]});Q23=makeQuery(id+"F0.imprint","IMPRINT",FACE,{"disambiguationData":[TD([[makeQuery(id+"F0.imprint","IMPRINT",EDGE,{"disambiguationData":[TD([[subQ2,-1.0]])],"derivedFrom":subQ1}),-1.0]])]});}
            var Q24;
            {var subQ0=sQuery(id+"F0.wireOp",EDGE,"E120");var subQ1=sQuery(id+"F0.wireOp",EDGE,"E49");var subQ2=makeQuery(id+"F0.imprint","INTERSECT",VERTEX,{"derivedFrom":[subQ1,subQ0]});Q24=makeQuery(id+"F0.imprint","IMPRINT",FACE,{"disambiguationData":[TD([[makeQuery(id+"F0.imprint","IMPRINT",EDGE,{"disambiguationData":[TD([[subQ2,-1.0]])],"derivedFrom":subQ1}),1.0]])]});}
            var Q25;
            {var subQ1=sQuery(id+"F0.wireOp",EDGE,"E15");var subQ8=makeQuery(id+"F0.imprint","INTERSECT",VERTEX,{"derivedFrom":[subQ1,sQuery(id+"F0.wireOp",EDGE,"E19")]});Q25=makeQuery(id+"F0.imprint","IMPRINT",FACE,{"disambiguationData":[TD([[makeQuery(id+"F0.imprint","IMPRINT",EDGE,{"disambiguationData":[TD([[subQ8,1.0]])],"derivedFrom":subQ1}),1.0]])]});}
            var Q26;
            {var subQ5=sQuery(id+"F0.wireOp",EDGE,"E39.filletArc");Q26=makeQuery(id+"F0.imprint","IMPRINT",FACE,{"disambiguationData":[TD([[makeQuery(id+"F0.imprint","IMPRINT",EDGE,{"derivedFrom":subQ5}),1.0]])]});}
            var Q27;
            {var subQ0=sQuery(id+"F0.wireOp",EDGE,"E6");var subQ1=sQuery(id+"F0.wireOp",EDGE,"E4");var subQ2=makeQuery(id+"F0.imprint","INTERSECT",VERTEX,{"disambiguationData":[OD(0.0)],"derivedFrom":[subQ1,subQ0]});Q27=makeQuery(id+"F0.imprint","IMPRINT",FACE,{"disambiguationData":[TD([[makeQuery(id+"F0.imprint","IMPRINT",EDGE,{"disambiguationData":[TD([[subQ2,1.0]])],"derivedFrom":subQ1}),1.0]])]});}
            var Q28;
            Q28=makeQuery(id+"F0.imprint","IMPRINT",FACE,{"disambiguationData":[TD([[makeQuery(id+"F0.imprint","IMPRINT",EDGE,{"derivedFrom":sQuery(id+"F0.wireOp",EDGE,"E107")}),-1.0]])]});
            var Q29;
            {var subQ0=sQuery(id+"F0.wireOp",EDGE,"E121");var subQ1=sQuery(id+"F0.wireOp",EDGE,"E4");var subQ2=makeQuery(id+"F0.imprint","INTERSECT",VERTEX,{"disambiguationData":[OD(0.0)],"derivedFrom":[subQ1,subQ0]});Q29=makeQuery(id+"F0.imprint","IMPRINT",FACE,{"disambiguationData":[TD([[makeQuery(id+"F0.imprint","IMPRINT",EDGE,{"disambiguationData":[TD([[subQ2,1.0]])],"derivedFrom":subQ1}),1.0]])]});}
            var Q30;
            {var subQ0=sQuery(id+"F0.wireOp",EDGE,"E8");Q30=makeQuery(id+"F0.imprint","IMPRINT",FACE,{"disambiguationData":[TD([[makeQuery(id+"F0.imprint","IMPRINT",EDGE,{"derivedFrom":subQ0}),-1.0]])]});}
            var Q31;
            {var subQ0=sQuery(id+"F0.wireOp",EDGE,"E17");var subQ1=sQuery(id+"F0.wireOp",EDGE,"E15");var subQ2=makeQuery(id+"F0.imprint","INTERSECT",VERTEX,{"disambiguationData":[OD(0.0)],"derivedFrom":[subQ1,subQ0]});Q31=makeQuery(id+"F0.imprint","IMPRINT",FACE,{"disambiguationData":[TD([[makeQuery(id+"F0.imprint","IMPRINT",EDGE,{"disambiguationData":[TD([[subQ2,-1.0]])],"derivedFrom":subQ1}),1.0]])]});}
            var Q32;
            {var subQ0=sQuery(id+"F0.wireOp",EDGE,"E6");var subQ1=sQuery(id+"F0.wireOp",EDGE,"E3");var subQ2=makeQuery(id+"F0.imprint","INTERSECT",VERTEX,{"disambiguationData":[OD(1.0)],"derivedFrom":[subQ1,subQ0]});Q32=makeQuery(id+"F0.imprint","IMPRINT",FACE,{"disambiguationData":[TD([[makeQuery(id+"F0.imprint","IMPRINT",EDGE,{"disambiguationData":[TD([[subQ2,-1.0]])],"derivedFrom":subQ1}),-1.0]])]});}
            var Q33;
            {var subQ5=sQuery(id+"F0.wireOp",EDGE,"E8");Q33=makeQuery(id+"F0.imprint","IMPRINT",FACE,{"disambiguationData":[TD([[makeQuery(id+"F0.imprint","IMPRINT",EDGE,{"derivedFrom":subQ5}),1.0]])]});}
            var Q34;
            {var subQ0=sQuery(id+"F0.wireOp",EDGE,"E18");Q34=makeQuery(id+"F0.imprint","IMPRINT",FACE,{"disambiguationData":[TD([[makeQuery(id+"F0.imprint","IMPRINT",EDGE,{"derivedFrom":subQ0}),1.0]])]});}
            var Q35;
            {var subQ0=sQuery(id+"F0.wireOp",EDGE,"E19");Q35=makeQuery(id+"F0.imprint","IMPRINT",FACE,{"disambiguationData":[TD([[makeQuery(id+"F0.imprint","IMPRINT",EDGE,{"derivedFrom":subQ0}),-1.0]])]});}
            var Q36;
            {var subQ13=sQuery(id+"F0.wireOp",EDGE,"E40.filletArc");Q36=makeQuery(id+"F0.imprint","IMPRINT",FACE,{"disambiguationData":[TD([[makeQuery(id+"F0.imprint","IMPRINT",EDGE,{"derivedFrom":subQ13}),-1.0]])]});}
            var Q37;
            Q37=makeQuery(id+"F0.imprint","IMPRINT",FACE,{"disambiguationData":[TD([[makeQuery(id+"F0.imprint","IMPRINT",EDGE,{"derivedFrom":sQuery(id+"F0.wireOp",EDGE,"E7")}),-1.0]])]});
            var Q38;
            {var subQ0=sQuery(id+"F0.wireOp",EDGE,"E160.filletArc");Q38=makeQuery(id+"F0.imprint","IMPRINT",FACE,{"disambiguationData":[TD([[makeQuery(id+"F0.imprint","IMPRINT",EDGE,{"derivedFrom":subQ0}),1.0]])]});}
            extrude(context, id + "F1", {"entities" : qUnion([Q0, Q1, Q2, Q3, Q4, Q5, Q6, Q7, Q8, Q9, Q10, Q11, Q12, Q13, Q14, Q15, Q16, Q17, Q18, Q19, Q20, Q21, Q22, Q23, Q24, Q25, Q26, Q27, Q28, Q29, Q30, Q31, Q32, Q33, Q34, Q35, Q36, Q37, Q38]), "oppositeDirection" : true, "depth" : 3 * mm, "offsetDistance" : 25 * mm});
        }
        {
            var Q0;
            Q0=makeQuery(id+"F0.imprint","IMPRINT",FACE,{"disambiguationData":[TD([[makeQuery(id+"F0.imprint","IMPRINT",EDGE,{"derivedFrom":sQuery(id+"F0.wireOp",EDGE,"E5")}),-1.0]])]});
            var Q1;
            Q1=makeQuery(id+"F0.imprint","IMPRINT",FACE,{"disambiguationData":[TD([[makeQuery(id+"F0.imprint","IMPRINT",EDGE,{"derivedFrom":sQuery(id+"F0.wireOp",EDGE,"E7")}),-1.0]])]});
            var Q2;
            {var subQ0=sQuery(id+"F0.wireOp",EDGE,"E39.filletArc");Q2=makeQuery(id+"F0.imprint","IMPRINT",FACE,{"disambiguationData":[TD([[makeQuery(id+"F0.imprint","IMPRINT",EDGE,{"derivedFrom":subQ0}),-1.0]])]});}
            var Q3;
            {var subQ13=sQuery(id+"F0.wireOp",EDGE,"E40.filletArc");Q3=makeQuery(id+"F0.imprint","IMPRINT",FACE,{"disambiguationData":[TD([[makeQuery(id+"F0.imprint","IMPRINT",EDGE,{"derivedFrom":subQ13}),-1.0]])]});}
            var Q4;
            {var subQ0=sQuery(id+"F0.wireOp",EDGE,"E172.filletArc");Q4=makeQuery(id+"F0.imprint","IMPRINT",FACE,{"disambiguationData":[TD([[makeQuery(id+"F0.imprint","IMPRINT",EDGE,{"derivedFrom":subQ0}),-1.0]])]});}
            var Q5;
            {var subQ0=sQuery(id+"F0.wireOp",EDGE,"E171.filletArc");Q5=makeQuery(id+"F0.imprint","IMPRINT",FACE,{"disambiguationData":[TD([[makeQuery(id+"F0.imprint","IMPRINT",EDGE,{"derivedFrom":subQ0}),-1.0]])]});}
            var Q6;
            {var subQ0=sQuery(id+"F0.wireOp",EDGE,"E121");var subQ1=sQuery(id+"F0.wireOp",EDGE,"E50");var subQ2=makeQuery(id+"F0.imprint","INTERSECT",VERTEX,{"derivedFrom":[subQ1,subQ0]});Q6=makeQuery(id+"F0.imprint","IMPRINT",FACE,{"disambiguationData":[TD([[makeQuery(id+"F0.imprint","IMPRINT",EDGE,{"disambiguationData":[TD([[subQ2,-1.0]])],"derivedFrom":subQ1}),-1.0]])]});}
            var Q7;
            {var subQ0=sQuery(id+"F0.wireOp",EDGE,"E160.filletArc");Q7=makeQuery(id+"F0.imprint","IMPRINT",FACE,{"disambiguationData":[TD([[makeQuery(id+"F0.imprint","IMPRINT",EDGE,{"derivedFrom":subQ0}),1.0]])]});}
            var Q8;
            {var subQ0=sQuery(id+"F0.wireOp",EDGE,"E160.filletArc");Q8=makeQuery(id+"F0.imprint","IMPRINT",FACE,{"disambiguationData":[TD([[makeQuery(id+"F0.imprint","IMPRINT",EDGE,{"derivedFrom":subQ0}),-1.0]])]});}
            var Q9;
            {var subQ0=sQuery(id+"F0.wireOp",EDGE,"E159.filletArc");Q9=makeQuery(id+"F0.imprint","IMPRINT",FACE,{"disambiguationData":[TD([[makeQuery(id+"F0.imprint","IMPRINT",EDGE,{"derivedFrom":subQ0}),-1.0]])]});}
            extrude(context, id + "F2", {"entities" : qUnion([Q0, Q1, Q2, Q3, Q4, Q5, Q6, Q7, Q8, Q9]), "depth" : 3 * mm, "offsetDistance" : 25 * mm});
        }
        {
            var Q0;
            Q0=makeQuery(id+"F0.imprint","IMPRINT",FACE,{"disambiguationData":[TD([[makeQuery(id+"F0.imprint","IMPRINT",EDGE,{"derivedFrom":sQuery(id+"F0.wireOp",EDGE,"E109")}),1.0]])]});
            var Q1;
            {var subQ0=sQuery(id+"F0.wireOp",EDGE,"E159.filletArc");Q1=makeQuery(id+"F0.imprint","IMPRINT",FACE,{"disambiguationData":[TD([[makeQuery(id+"F0.imprint","IMPRINT",EDGE,{"derivedFrom":subQ0}),-1.0]])]});}
            var Q2;
            {var subQ7=sQuery(id+"F0.wireOp",EDGE,"E176");Q2=makeQuery(id+"F0.imprint","IMPRINT",FACE,{"disambiguationData":[TD([[makeQuery(id+"F0.imprint","IMPRINT",EDGE,{"derivedFrom":subQ7}),-1.0]])]});}
            var Q3;
            {var subQ0=sQuery(id+"F0.wireOp",EDGE,"E160.filletArc");Q3=makeQuery(id+"F0.imprint","IMPRINT",FACE,{"disambiguationData":[TD([[makeQuery(id+"F0.imprint","IMPRINT",EDGE,{"derivedFrom":subQ0}),-1.0]])]});}
            var Q4;
            {var subQ0=sQuery(id+"F0.wireOp",EDGE,"E151");Q4=makeQuery(id+"F0.imprint","IMPRINT",FACE,{"disambiguationData":[TD([[makeQuery(id+"F0.imprint","IMPRINT",EDGE,{"derivedFrom":subQ0}),-1.0]])]});}
            var Q5;
            {var subQ0=sQuery(id+"F0.wireOp",EDGE,"E152");Q5=makeQuery(id+"F0.imprint","IMPRINT",FACE,{"disambiguationData":[TD([[makeQuery(id+"F0.imprint","IMPRINT",EDGE,{"derivedFrom":subQ0}),1.0]])]});}
            var Q6;
            {var subQ0=sQuery(id+"F0.wireOp",EDGE,"E171.filletArc");Q6=makeQuery(id+"F0.imprint","IMPRINT",FACE,{"disambiguationData":[TD([[makeQuery(id+"F0.imprint","IMPRINT",EDGE,{"derivedFrom":subQ0}),-1.0]])]});}
            var Q7;
            {var subQ0=sQuery(id+"F0.wireOp",EDGE,"E163");Q7=makeQuery(id+"F0.imprint","IMPRINT",FACE,{"disambiguationData":[TD([[makeQuery(id+"F0.imprint","IMPRINT",EDGE,{"derivedFrom":subQ0}),-1.0]])]});}
            var Q8;
            {var subQ1=sQuery(id+"F0.wireOp",EDGE,"E164");Q8=makeQuery(id+"F0.imprint","IMPRINT",FACE,{"disambiguationData":[TD([[makeQuery(id+"F0.imprint","IMPRINT",EDGE,{"derivedFrom":subQ1}),1.0]])]});}
            var Q9;
            {var subQ0=sQuery(id+"F0.wireOp",EDGE,"E172.filletArc");Q9=makeQuery(id+"F0.imprint","IMPRINT",FACE,{"disambiguationData":[TD([[makeQuery(id+"F0.imprint","IMPRINT",EDGE,{"derivedFrom":subQ0}),-1.0]])]});}
            var Q10;
            Q10=makeQuery(id+"F0.imprint","IMPRINT",FACE,{"disambiguationData":[TD([[makeQuery(id+"F0.imprint","IMPRINT",EDGE,{"derivedFrom":sQuery(id+"F0.wireOp",EDGE,"E110")}),-1.0]])]});
            var Q11;
            {var subQ0=sQuery(id+"F0.wireOp",EDGE,"E58");Q11=makeQuery(id+"F0.imprint","IMPRINT",FACE,{"disambiguationData":[TD([[makeQuery(id+"F0.imprint","IMPRINT",EDGE,{"derivedFrom":subQ0}),-1.0]])]});}
            var Q12;
            {var subQ0=sQuery(id+"F0.wireOp",EDGE,"E184.filletArc");Q12=makeQuery(id+"F0.imprint","IMPRINT",FACE,{"disambiguationData":[TD([[makeQuery(id+"F0.imprint","IMPRINT",EDGE,{"derivedFrom":subQ0}),1.0]])]});}
            var Q13;
            {var subQ0=sQuery(id+"F0.wireOp",EDGE,"E57");Q13=makeQuery(id+"F0.imprint","IMPRINT",FACE,{"disambiguationData":[TD([[makeQuery(id+"F0.imprint","IMPRINT",EDGE,{"derivedFrom":subQ0}),1.0]])]});}
            extrude(context, id + "F3", {"entities" : qUnion([Q0, Q1, Q2, Q3, Q4, Q5, Q6, Q7, Q8, Q9, Q10, Q11, Q12, Q13]), "oppositeDirection" : true, "depth" : 3 * mm, "offsetDistance" : 25 * mm});
        }
        {
            var Q0;
            {var subQ0=sQuery(id+"F0.wireOp",EDGE,"E57");Q0=makeQuery(id+"F0.imprint","IMPRINT",FACE,{"disambiguationData":[TD([[makeQuery(id+"F0.imprint","IMPRINT",EDGE,{"derivedFrom":subQ0}),1.0]])]});}
            var Q1;
            {var subQ0=sQuery(id+"F0.wireOp",EDGE,"E183.filletArc");Q1=makeQuery(id+"F0.imprint","IMPRINT",FACE,{"disambiguationData":[TD([[makeQuery(id+"F0.imprint","IMPRINT",EDGE,{"derivedFrom":subQ0}),-1.0]])]});}
            var Q2;
            {var subQ0=sQuery(id+"F0.wireOp",EDGE,"E184.filletArc");Q2=makeQuery(id+"F0.imprint","IMPRINT",FACE,{"disambiguationData":[TD([[makeQuery(id+"F0.imprint","IMPRINT",EDGE,{"derivedFrom":subQ0}),-1.0]])]});}
            var Q3;
            {var subQ0=sQuery(id+"F0.wireOp",EDGE,"E184.filletArc");Q3=makeQuery(id+"F0.imprint","IMPRINT",FACE,{"disambiguationData":[TD([[makeQuery(id+"F0.imprint","IMPRINT",EDGE,{"derivedFrom":subQ0}),1.0]])]});}
            var Q4;
            {var subQ0=sQuery(id+"F0.wireOp",EDGE,"E195.filletArc");Q4=makeQuery(id+"F0.imprint","IMPRINT",FACE,{"disambiguationData":[TD([[makeQuery(id+"F0.imprint","IMPRINT",EDGE,{"derivedFrom":subQ0}),-1.0]])]});}
            var Q5;
            {var subQ0=sQuery(id+"F0.wireOp",EDGE,"E196.filletArc");Q5=makeQuery(id+"F0.imprint","IMPRINT",FACE,{"disambiguationData":[TD([[makeQuery(id+"F0.imprint","IMPRINT",EDGE,{"derivedFrom":subQ0}),-1.0]])]});}
            var Q6;
            {var subQ0=sQuery(id+"F0.wireOp",EDGE,"E58");Q6=makeQuery(id+"F0.imprint","IMPRINT",FACE,{"disambiguationData":[TD([[makeQuery(id+"F0.imprint","IMPRINT",EDGE,{"derivedFrom":subQ0}),-1.0]])]});}
            extrude(context, id + "F4", {"entities" : qUnion([Q0, Q1, Q2, Q3, Q4, Q5, Q6]), "depth" : 3 * mm, "offsetDistance" : 25 * mm});
        }
        {
            var Q0;
            Q0=makeQuery(id+"F0.imprint","IMPRINT",FACE,{"disambiguationData":[TD([[makeQuery(id+"F0.imprint","IMPRINT",EDGE,{"derivedFrom":sQuery(id+"F0.wireOp",EDGE,"E60")}),1.0]])]});
            var Q1;
            Q1=makeQuery(id+"F0.imprint","IMPRINT",FACE,{"disambiguationData":[TD([[makeQuery(id+"F0.imprint","IMPRINT",EDGE,{"derivedFrom":sQuery(id+"F0.wireOp",EDGE,"E59")}),-1.0]])]});
            var Q2;
            {var subQ9=sQuery(id+"F0.wireOp",EDGE,"E57");Q2=makeQuery(id+"F0.imprint","IMPRINT",FACE,{"disambiguationData":[TD([[makeQuery(id+"F0.imprint","IMPRINT",EDGE,{"derivedFrom":subQ9}),-1.0]])]});}
            var Q3;
            {var subQ0=sQuery(id+"F0.wireOp",EDGE,"E208.filletArc");Q3=makeQuery(id+"F0.imprint","IMPRINT",FACE,{"disambiguationData":[TD([[makeQuery(id+"F0.imprint","IMPRINT",EDGE,{"derivedFrom":subQ0}),1.0]])]});}
            var Q4;
            {var subQ3=sQuery(id+"F0.wireOp",EDGE,"E58");Q4=makeQuery(id+"F0.imprint","IMPRINT",FACE,{"disambiguationData":[TD([[makeQuery(id+"F0.imprint","IMPRINT",EDGE,{"derivedFrom":subQ3}),1.0]])]});}
            var Q5;
            Q5=makeQuery(id+"F0.imprint","IMPRINT",FACE,{"disambiguationData":[TD([[makeQuery(id+"F0.imprint","IMPRINT",EDGE,{"derivedFrom":sQuery(id+"F0.wireOp",EDGE,"E61")}),-1.0]])]});
            var Q6;
            Q6=makeQuery(id+"F0.imprint","IMPRINT",FACE,{"disambiguationData":[TD([[makeQuery(id+"F0.imprint","IMPRINT",EDGE,{"derivedFrom":sQuery(id+"F0.wireOp",EDGE,"E61")}),1.0]])]});
            var Q7;
            {var subQ0=sQuery(id+"F0.wireOp",EDGE,"E183.filletArc");Q7=makeQuery(id+"F0.imprint","IMPRINT",FACE,{"disambiguationData":[TD([[makeQuery(id+"F0.imprint","IMPRINT",EDGE,{"derivedFrom":subQ0}),-1.0]])]});}
            var Q8;
            {var subQ0=sQuery(id+"F0.wireOp",EDGE,"E175");Q8=makeQuery(id+"F0.imprint","IMPRINT",FACE,{"disambiguationData":[TD([[makeQuery(id+"F0.imprint","IMPRINT",EDGE,{"derivedFrom":subQ0}),-1.0]])]});}
            var Q9;
            {var subQ1=sQuery(id+"F0.wireOp",EDGE,"E176");Q9=makeQuery(id+"F0.imprint","IMPRINT",FACE,{"disambiguationData":[TD([[makeQuery(id+"F0.imprint","IMPRINT",EDGE,{"derivedFrom":subQ1}),1.0]])]});}
            var Q10;
            {var subQ0=sQuery(id+"F0.wireOp",EDGE,"E184.filletArc");Q10=makeQuery(id+"F0.imprint","IMPRINT",FACE,{"disambiguationData":[TD([[makeQuery(id+"F0.imprint","IMPRINT",EDGE,{"derivedFrom":subQ0}),-1.0]])]});}
            var Q11;
            {var subQ0=sQuery(id+"F0.wireOp",EDGE,"E195.filletArc");Q11=makeQuery(id+"F0.imprint","IMPRINT",FACE,{"disambiguationData":[TD([[makeQuery(id+"F0.imprint","IMPRINT",EDGE,{"derivedFrom":subQ0}),-1.0]])]});}
            var Q12;
            {var subQ0=sQuery(id+"F0.wireOp",EDGE,"E196.filletArc");Q12=makeQuery(id+"F0.imprint","IMPRINT",FACE,{"disambiguationData":[TD([[makeQuery(id+"F0.imprint","IMPRINT",EDGE,{"derivedFrom":subQ0}),-1.0]])]});}
            var Q13;
            {var subQ0=sQuery(id+"F0.wireOp",EDGE,"E187");Q13=makeQuery(id+"F0.imprint","IMPRINT",FACE,{"disambiguationData":[TD([[makeQuery(id+"F0.imprint","IMPRINT",EDGE,{"derivedFrom":subQ0}),-1.0]])]});}
            var Q14;
            {var subQ1=sQuery(id+"F0.wireOp",EDGE,"E188");Q14=makeQuery(id+"F0.imprint","IMPRINT",FACE,{"disambiguationData":[TD([[makeQuery(id+"F0.imprint","IMPRINT",EDGE,{"derivedFrom":subQ1}),1.0]])]});}
            extrude(context, id + "F5", {"entities" : qUnion([Q0, Q1, Q2, Q3, Q4, Q5, Q6, Q7, Q8, Q9, Q10, Q11, Q12, Q13, Q14]), "oppositeDirection" : true, "depth" : 3 * mm, "offsetDistance" : 25 * mm});
        }
        {
            var Q0;
            {var subQ9=sQuery(id+"F0.wireOp",EDGE,"E57");Q0=makeQuery(id+"F0.imprint","IMPRINT",FACE,{"disambiguationData":[TD([[makeQuery(id+"F0.imprint","IMPRINT",EDGE,{"derivedFrom":subQ9}),-1.0]])]});}
            var Q1;
            {var subQ0=sQuery(id+"F0.wireOp",EDGE,"E207.filletArc");Q1=makeQuery(id+"F0.imprint","IMPRINT",FACE,{"disambiguationData":[TD([[makeQuery(id+"F0.imprint","IMPRINT",EDGE,{"derivedFrom":subQ0}),-1.0]])]});}
            var Q2;
            {var subQ0=sQuery(id+"F0.wireOp",EDGE,"E208.filletArc");Q2=makeQuery(id+"F0.imprint","IMPRINT",FACE,{"disambiguationData":[TD([[makeQuery(id+"F0.imprint","IMPRINT",EDGE,{"derivedFrom":subQ0}),-1.0]])]});}
            var Q3;
            {var subQ0=sQuery(id+"F0.wireOp",EDGE,"E208.filletArc");Q3=makeQuery(id+"F0.imprint","IMPRINT",FACE,{"disambiguationData":[TD([[makeQuery(id+"F0.imprint","IMPRINT",EDGE,{"derivedFrom":subQ0}),1.0]])]});}
            var Q4;
            {var subQ0=sQuery(id+"F0.wireOp",EDGE,"E219.filletArc");Q4=makeQuery(id+"F0.imprint","IMPRINT",FACE,{"disambiguationData":[TD([[makeQuery(id+"F0.imprint","IMPRINT",EDGE,{"derivedFrom":subQ0}),-1.0]])]});}
            var Q5;
            {var subQ0=sQuery(id+"F0.wireOp",EDGE,"E220.filletArc");Q5=makeQuery(id+"F0.imprint","IMPRINT",FACE,{"disambiguationData":[TD([[makeQuery(id+"F0.imprint","IMPRINT",EDGE,{"derivedFrom":subQ0}),-1.0]])]});}
            var Q6;
            {var subQ3=sQuery(id+"F0.wireOp",EDGE,"E58");Q6=makeQuery(id+"F0.imprint","IMPRINT",FACE,{"disambiguationData":[TD([[makeQuery(id+"F0.imprint","IMPRINT",EDGE,{"derivedFrom":subQ3}),1.0]])]});}
            var Q7;
            Q7=makeQuery(id+"F0.imprint","IMPRINT",FACE,{"disambiguationData":[TD([[makeQuery(id+"F0.imprint","IMPRINT",EDGE,{"derivedFrom":sQuery(id+"F0.wireOp",EDGE,"E61")}),-1.0]])]});
            extrude(context, id + "F6", {"entities" : qUnion([Q0, Q1, Q2, Q3, Q4, Q5, Q6, Q7]), "depth" : 3 * mm, "offsetDistance" : 25 * mm});
        }
    });
